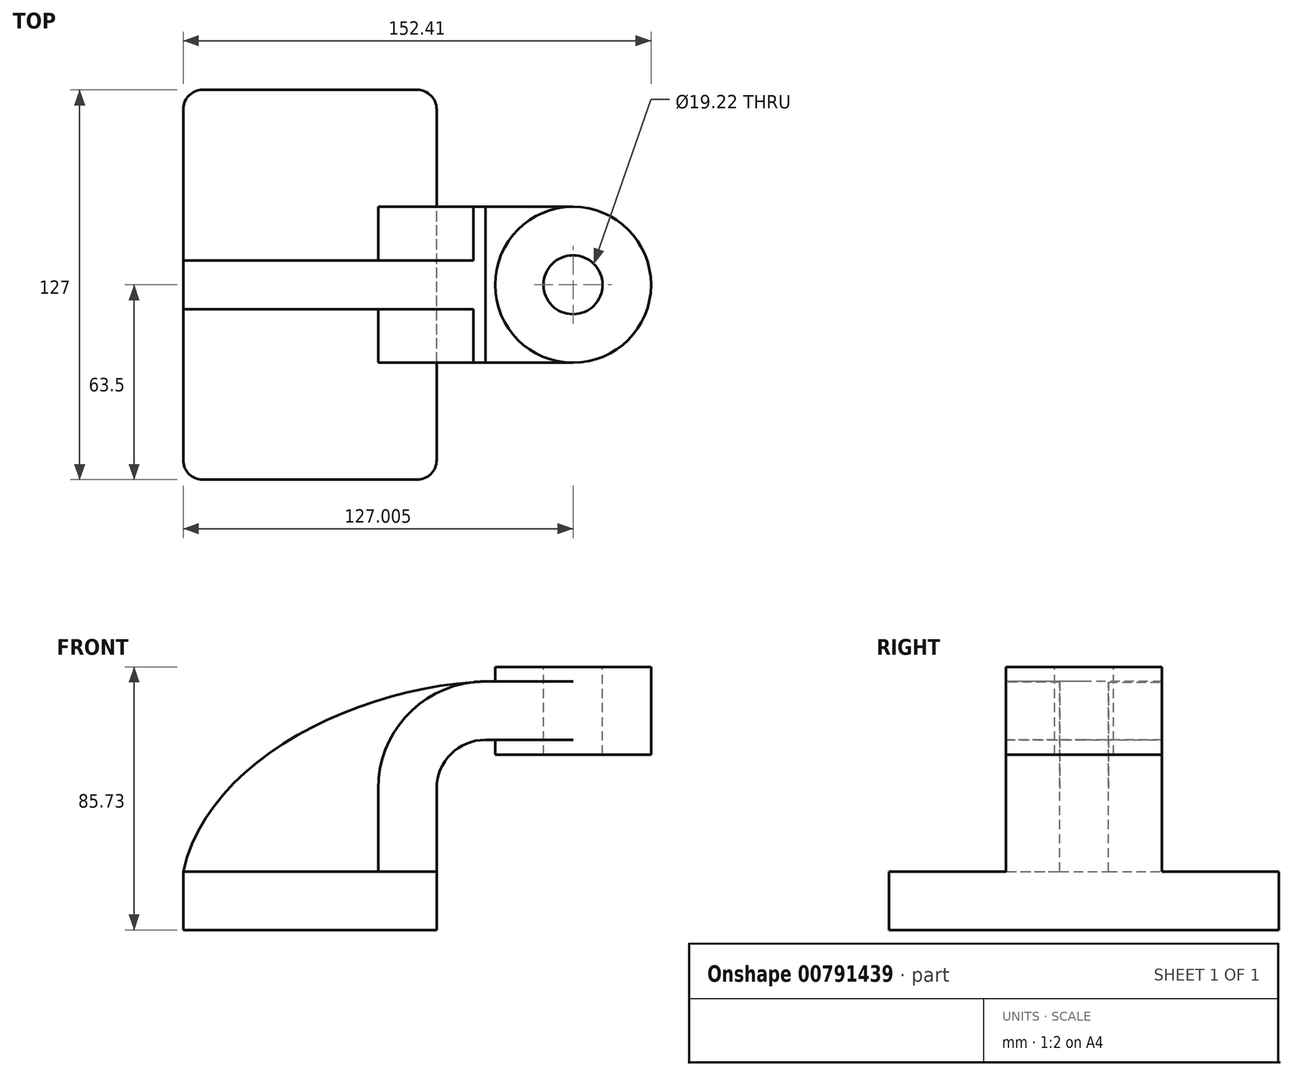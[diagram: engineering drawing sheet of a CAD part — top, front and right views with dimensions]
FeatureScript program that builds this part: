
annotation { "Feature Type Name" : "Feature", "Feature Type Description" : "" }
export const myFeature = defineFeature(function(context is Context, id is Id, definition is map)
    precondition{}
    {
        {
            var Q0;
            Q0=qCreatedBy(makeId("Front.planeOp"),FACE);
            var sketch = newSketch(context, id + "F0", { "sketchPlane" : qUnion([Q0])});
            skLineSegment(sketch, "E0.bottom", {"start": v(-41.27, -9.52) * mm, "end": v(41.28, -9.52) * mm});
            skLineSegment(sketch, "E0.top", {"start": v(-41.28, 9.53) * mm, "end": v(41.27, 9.53) * mm});
            skLineSegment(sketch, "E0.left", {"start": v(-41.27, -9.52) * mm, "end": v(-41.28, 9.53) * mm});
            skLineSegment(sketch, "E0.right", {"start": v(41.28, -9.52) * mm, "end": v(41.27, 9.53) * mm});
            skPoint(sketch, "E0.middle", {"position": v(0, 0) * mm});
            skLineSegment(sketch, "E1.bottom", {"start": v(111.12, 47.63) * mm, "end": v(60.32, 47.63) * mm});
            skLineSegment(sketch, "E1.top", {"start": v(111.13, 76.2) * mm, "end": v(60.33, 76.2) * mm});
            skLineSegment(sketch, "E1.left", {"start": v(111.12, 47.62) * mm, "end": v(111.12, 76.2) * mm});
            skLineSegment(sketch, "E1.right", {"start": v(60.32, 47.63) * mm, "end": v(60.32, 76.2) * mm});
            skPoint(sketch, "E1.middle", {"position": v(85.72, 61.91) * mm});
            skLineSegment(sketch, "E2", {"start": v(41.27, 9.53) * mm, "end": v(41.27, 36.53) * mm});
            skArc(sketch, "E3", {"start": v(41.27, 36.53) * mm, "mid": v(45.92, 47.75) * mm, "end": v(57.15, 52.4) * mm});
            skLineSegment(sketch, "E4", {"start": v(57.15, 52.4) * mm, "end": v(92.4, 52.4) * mm});
            skLineSegment(sketch, "E5.0", {"start": v(57.15, 71.45) * mm, "end": v(92.4, 71.45) * mm});
            skArc(sketch, "E5.1", {"start": v(22.22, 36.53) * mm, "mid": v(32.45, 61.22) * mm, "end": v(57.15, 71.45) * mm});
            skLineSegment(sketch, "E5.2", {"start": v(22.22, 9.53) * mm, "end": v(22.22, 36.53) * mm});
            skLineSegment(sketch, "E6", {"start": v(85.72, 61.91) * mm, "end": v(85.72, 76.2) * mm});
            skLineSegment(sketch, "E7", {"start": v(85.72, 47.63) * mm, "end": v(85.72, 61.91) * mm});
            skFitSpline(sketch, "E8", {"points": [v(-41.28, 9.53) * mm, v(57.15, 71.45) * mm], "startDerivative": vector(24.1, 109.53) * mm, "endDerivative": vector(125.2, 5.04) * mm});
            skSolve(sketch);
        }
        {
            var Q0;
            Q0=makeQuery(id+"F0.imprint","IMPRINT",FACE,{"disambiguationData":[TD([[makeQuery(id+"F0.imprint","IMPRINT",EDGE,{"derivedFrom":sQuery(id+"F0.wireOp",EDGE,"E0.bottom")}),1.0]])]});
            extrude(context, id + "F1", {"entities" : qUnion([Q0]), "endBound" : BoundingType.SYMMETRIC, "depth" : 127 * mm, "offsetDistance" : 25.4 * mm});
        }
        {
            var Q0;
            {var subQ1=sQuery(id+"F0.wireOp",EDGE,"E2");Q0=makeQuery(id+"F0.imprint","IMPRINT",FACE,{"disambiguationData":[TD([[makeQuery(id+"F0.imprint","IMPRINT",EDGE,{"derivedFrom":subQ1}),1.0]])]});}
            var Q1;
            {var subQ5=sQuery(id+"F0.wireOp",EDGE,"E4");var subQ6=sQuery(id+"F0.wireOp",EDGE,"E1.right");var subQ7=makeQuery(id+"F0.imprint","INTERSECT",VERTEX,{"derivedFrom":[subQ6,subQ5]});Q1=makeQuery(id+"F0.imprint","IMPRINT",FACE,{"disambiguationData":[TD([[makeQuery(id+"F0.imprint","IMPRINT",EDGE,{"disambiguationData":[TD([[subQ7,-1.0]])],"derivedFrom":subQ6}),-1.0]])]});}
            extrude(context, id + "F2", {"entities" : qUnion([Q0, Q1]), "operationType" : NewBodyOperationType.ADD, "endBound" : BoundingType.SYMMETRIC, "depth" : 50.8 * mm, "offsetDistance" : 25.4 * mm});
        }
        {
            var Q0;
            {var subQ3=sQuery(id+"F0.wireOp",EDGE,"E5.2");Q0=makeQuery(id+"F0.imprint","IMPRINT",FACE,{"disambiguationData":[TD([[makeQuery(id+"F0.imprint","IMPRINT",EDGE,{"derivedFrom":subQ3}),1.0]])]});}
            extrude(context, id + "F3", {"entities" : qUnion([Q0]), "operationType" : NewBodyOperationType.ADD, "endBound" : BoundingType.SYMMETRIC, "depth" : 15.88 * mm, "offsetDistance" : 25.4 * mm});
        }
        {
            var Q0;
            {var subQ0=sQuery(id+"F0.wireOp",EDGE,"E1.left");Q0=makeQuery(id+"F0.imprint","IMPRINT",FACE,{"disambiguationData":[TD([[makeQuery(id+"F0.imprint","IMPRINT",EDGE,{"derivedFrom":subQ0}),1.0]])]});}
            var Q1;
            Q1=sQuery(id+"F0.wireOp",EDGE,"E6");
            revolve(context, id + "F4", {"operationType" : NewBodyOperationType.ADD, "surfaceOperationType" : NewSurfaceOperationType.NEW, "entities" : qUnion([Q0]), "axis" : qUnion([Q1]), "revolveType" : RevolveType.FULL});
        }
        {
            var Q0;
            Q0=makeQuery(id+"F1.opExtrude","CAP_EDGE",EDGE,{"disambiguationData":[OSD([sQuery(id+"F0.wireOp",EDGE,"E0.right")])],"isStart":false});
            var Q1;
            Q1=makeQuery(id+"F1.opExtrude","CAP_EDGE",EDGE,{"disambiguationData":[OSD([sQuery(id+"F0.wireOp",EDGE,"E0.left")])],"isStart":false});
            var Q2;
            Q2=makeQuery(id+"F1.opExtrude","CAP_EDGE",EDGE,{"disambiguationData":[OSD([sQuery(id+"F0.wireOp",EDGE,"E0.right")])],"isStart":true});
            var Q3;
            Q3=makeQuery(id+"F1.opExtrude","CAP_EDGE",EDGE,{"disambiguationData":[OSD([sQuery(id+"F0.wireOp",EDGE,"E0.left")])],"isStart":true});
            fillet(context, id + "F5", {"entities" : qUnion([Q0, Q1, Q2, Q3]), "radius" : 6.35 * mm, "tangentPropagation" : true, "allowEdgeOverflow" : false});
        }
        {
            var Q0;
            Q0=makeQuery(id+"F4.opRevolve","SWEPT_FACE",FACE,{"disambiguationData":[OSD([sQuery(id+"F0.wireOp",EDGE,"E1.top")])]});
            var sketch = newSketch(context, id + "F6", { "sketchPlane" : qUnion([Q0])});
            skCircle(sketch, "E9", {"center": v(85.72, 0) * mm, "radius": 9.61 * mm});
            skSolve(sketch);
        }
        {
            var Q0;
            Q0=makeQuery(id+"F6.imprint","IMPRINT",FACE,{"disambiguationData":[TD([[makeQuery(id+"F6.imprint","IMPRINT",EDGE,{"derivedFrom":sQuery(id+"F6.wireOp",EDGE,"E9")}),1.0]])]});
            extrude(context, id + "F7", {"entities" : qUnion([Q0]), "operationType" : NewBodyOperationType.REMOVE, "endBound" : BoundingType.THROUGH_ALL, "oppositeDirection" : true, "depth" : 25.4 * mm, "offsetDistance" : 25.4 * mm});
        }
    });
